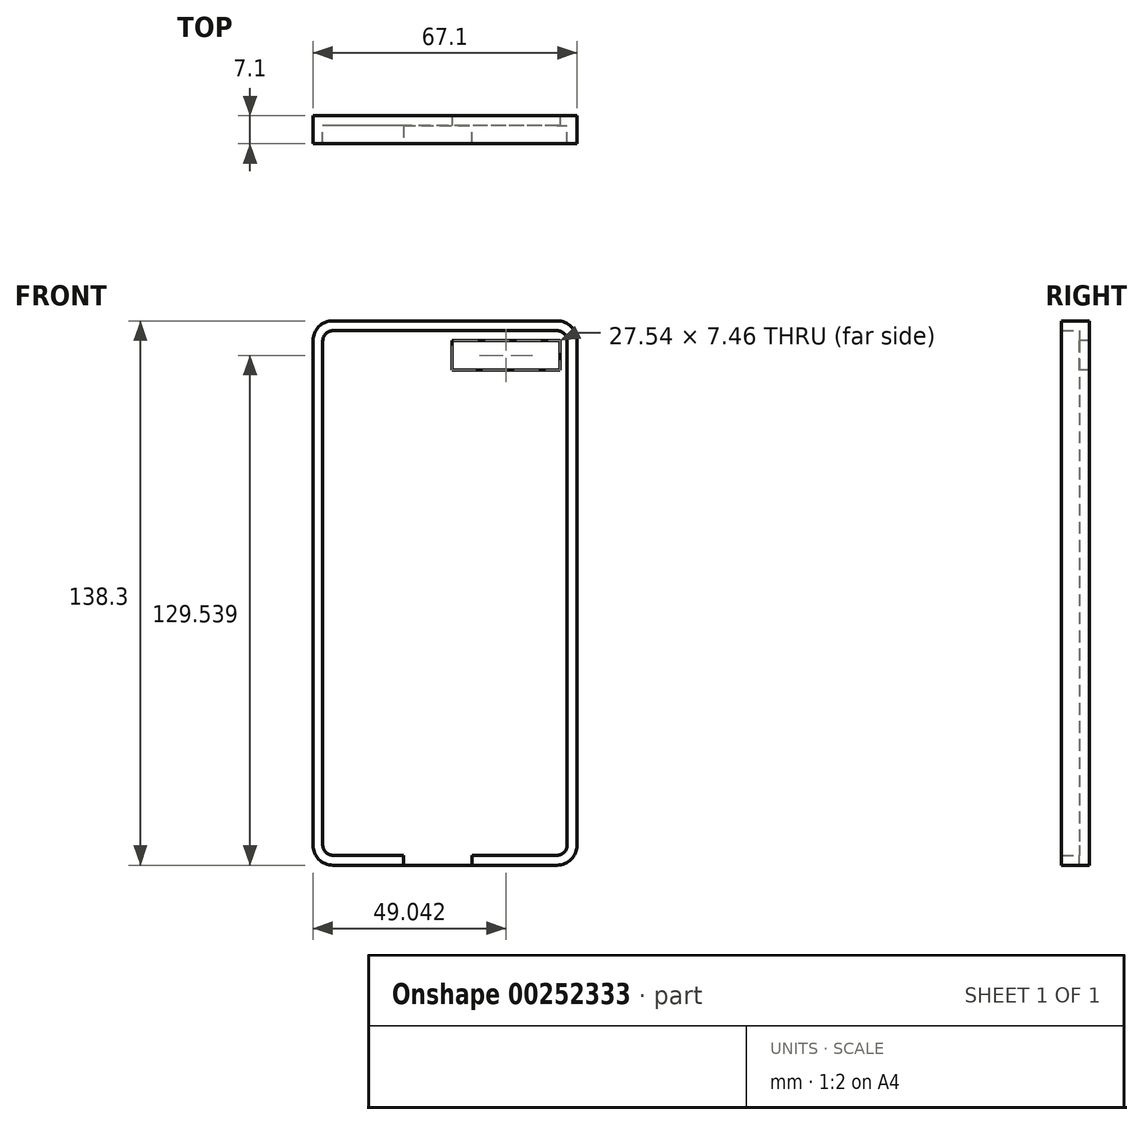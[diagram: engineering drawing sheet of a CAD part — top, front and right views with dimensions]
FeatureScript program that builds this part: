
annotation { "Feature Type Name" : "Feature", "Feature Type Description" : "" }
export const myFeature = defineFeature(function(context is Context, id is Id, definition is map)
    precondition{}
    {
        {
            var Q0;
            Q0=qCreatedBy(makeId("Front.planeOp"),FACE);
            var sketch = newSketch(context, id + "F0", { "sketchPlane" : qUnion([Q0])});
            skLineSegment(sketch, "E0.bottom", {"start": v(33.55, 69.15) * mm, "end": v(-33.55, 69.15) * mm});
            skLineSegment(sketch, "E0.top", {"start": v(33.55, -69.15) * mm, "end": v(-33.55, -69.15) * mm});
            skLineSegment(sketch, "E0.left", {"start": v(33.55, 69.15) * mm, "end": v(33.55, -69.15) * mm});
            skLineSegment(sketch, "E0.right", {"start": v(-33.55, 69.15) * mm, "end": v(-33.55, -69.15) * mm});
            skPoint(sketch, "E0.middle", {"position": v(0, 0) * mm});
            skSolve(sketch);
        }
        {
            var Q0;
            Q0=makeQuery(id+"F0.imprint","IMPRINT",FACE,{"disambiguationData":[TD([[makeQuery(id+"F0.imprint","IMPRINT",EDGE,{"derivedFrom":sQuery(id+"F0.wireOp",EDGE,"E0.bottom")}),1.0]])]});
            extrude(context, id + "F1", {"entities" : qUnion([Q0]), "endBound" : BoundingType.SYMMETRIC, "depth" : 7.1 * mm});
        }
        {
            var Q0;
            Q0=makeQuery(id+"F1.opExtrude","SWEPT_EDGE",EDGE,{"disambiguationData":[OSD([sQuery(id+"F0.wireOp",EDGE,"E0.bottom"),sQuery(id+"F0.wireOp",EDGE,"E0.right")])]});
            var Q1;
            Q1=makeQuery(id+"F1.opExtrude","SWEPT_EDGE",EDGE,{"disambiguationData":[OSD([sQuery(id+"F0.wireOp",EDGE,"E0.top"),sQuery(id+"F0.wireOp",EDGE,"E0.right")])]});
            var Q2;
            Q2=makeQuery(id+"F1.opExtrude","SWEPT_EDGE",EDGE,{"disambiguationData":[OSD([sQuery(id+"F0.wireOp",EDGE,"E0.top"),sQuery(id+"F0.wireOp",EDGE,"E0.left")])]});
            var Q3;
            Q3=makeQuery(id+"F1.opExtrude","SWEPT_EDGE",EDGE,{"disambiguationData":[OSD([sQuery(id+"F0.wireOp",EDGE,"E0.bottom"),sQuery(id+"F0.wireOp",EDGE,"E0.left")])]});
            fillet(context, id + "F2", {"entities" : qUnion([Q0, Q1, Q2, Q3]), "radius" : 5.08 * mm, "tangentPropagation" : true, "allowEdgeOverflow" : false});
        }
        {
            var Q0;
            Q0=makeQuery(id+"F1.opExtrude","CAP_FACE",FACE,{"disambiguationData":[OSD([sQuery(id+"F0.wireOp",EDGE,"E0.bottom"),sQuery(id+"F0.wireOp",EDGE,"E0.top"),sQuery(id+"F0.wireOp",EDGE,"E0.left"),sQuery(id+"F0.wireOp",EDGE,"E0.right")])],"isStart":false});
            shell(context, id + "F3", {"entities" : qUnion([Q0]), "thickness" : 2.5 * mm});
        }
        {
            var Q0;
            Q0=qCreatedBy(makeId("Front.planeOp"),FACE);
            var sketch = newSketch(context, id + "F4", { "sketchPlane" : qUnion([Q0])});
            skLineSegment(sketch, "E1.bottom", {"start": v(29.26, 56.66) * mm, "end": v(1.72, 56.66) * mm});
            skLineSegment(sketch, "E1.top", {"start": v(29.26, 64.12) * mm, "end": v(1.72, 64.12) * mm});
            skLineSegment(sketch, "E1.left", {"start": v(29.26, 56.66) * mm, "end": v(29.26, 64.12) * mm});
            skLineSegment(sketch, "E1.right", {"start": v(1.72, 56.66) * mm, "end": v(1.72, 64.12) * mm});
            skPoint(sketch, "E1.middle", {"position": v(15.5, 60.39) * mm});
            skSolve(sketch);
        }
        {
            var Q0;
            Q0=makeQuery(id+"F4.imprint","IMPRINT",FACE,{"disambiguationData":[TD([[makeQuery(id+"F4.imprint","IMPRINT",EDGE,{"derivedFrom":sQuery(id+"F4.wireOp",EDGE,"E1.bottom")}),-1.0]])]});
            extrude(context, id + "F5", {"entities" : qUnion([Q0]), "operationType" : NewBodyOperationType.REMOVE, "endBound" : BoundingType.SYMMETRIC, "oppositeDirection" : true, "depth" : 25 * mm});
        }
        {
            var Q0;
            Q0=makeQuery(id+"F3.opShell","OFFSET_FACE",FACE,{"disambiguationData":[OSD([sQuery(id+"F0.wireOp",EDGE,"E0.top")])]});
            var sketch = newSketch(context, id + "F6", { "sketchPlane" : qUnion([Q0])});
            skLineSegment(sketch, "E2.bottom", {"start": v(6.87, -3.55) * mm, "end": v(-10.54, -3.55) * mm});
            skLineSegment(sketch, "E2.top", {"start": v(6.87, 1.05) * mm, "end": v(-10.54, 1.05) * mm});
            skLineSegment(sketch, "E2.left", {"start": v(6.87, -3.55) * mm, "end": v(6.87, 1.05) * mm});
            skLineSegment(sketch, "E2.right", {"start": v(-10.54, -3.55) * mm, "end": v(-10.54, 1.05) * mm});
            skSolve(sketch);
        }
        {
            var Q0;
            Q0 = qSketchRegion(id + "F6", true);
            extrude(context, id + "F7", {"entities" : qUnion([Q0]), "operationType" : NewBodyOperationType.REMOVE, "oppositeDirection" : true, "depth" : 25 * mm});
        }
    });
